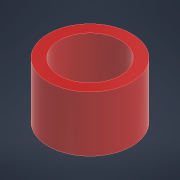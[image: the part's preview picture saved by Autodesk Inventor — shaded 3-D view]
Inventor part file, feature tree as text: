
AUTODESK INVENTOR PART (.ipt)
format: ipt  version: 2021 (Build 250183000, 183)  size: 105,984 bytes
history: native  units: mm
features: other x2, extrude x1, sketch x1
ambient origin geometry x8: Origin, YZ Plane, XZ Plane, XY Plane, X Axis, Y Axis, Z Axis, Center Point
bodies: Body1 (feature_tree)
feature tree (4):
  other  "Roda - Pneu"
  other  "Sólido1"
  extrude  "Extrusão1"  Depth=20.0mm
  sketch  "Esboço1"  dims[d0=22.0mm d1=30.0mm d2=20.0mm d3=0.0mm]
